# Revit family: Hager-VEGAD-Surface_mounted-IP30-Without_Cover-With_DIN-Hosted-FR-fr
name_source: partatom
category: Electrical Equipment
units: mm (PartAtom-declared; Revit-internal decimal feet)

## family parameters
Cut with Voids When Loaded = No
Host = Face
Maintain Annotation Orientation = Yes
Panel Configuration = Two Columns, Circuits Across
Part Type = Panelboard
Room Calculation Point = No
Round Connector Dimension = Use Diameter
Shared = No

## types (10) — shared parameters
BC_MODEL_ID = 1547015
BC_OBJECT_ID = 513439
BC_OBJECT_VERSION = #3
Code hager = ADD-EC000214_EU
EF000003 - mode de pose = saillie
EF000007 - couleur = blanc
EF000008 - largeur = 550 mm  [stored 1.80446 ft]
EF000024 - résistant aux UV = No
EF000049 - profondeur = 193 mm  [stored 0.633202 ft]
EF000116 - numéro RAL = 9010
EF000118 - avec cadre/support de montage = No
EF000218 - profondeur d'encastrement = 193 mm  [stored 0.633202 ft]
EF000846 - largeur d'encastrement = 550 mm  [stored 1.80446 ft]
EF001062 - finition CEM = No
EF001088 - possibilité de montage en saillie = Yes
EF001134 - rail DIN = Yes
EF002950 - largeur en nombre de modules = 24
EF005474 - indice de protection (IP) = IP30
EF006244 - couvercle/porte transparent(e) = No
EF006306 - avec serrure = No
EF009212 - finition du couvercle = avec échancrure
EF015776 - borne de mise à la terre = Yes
EF015777 - borne à conducteur neutre = No
EF015941 - porte pour transmission du signal = No
ETIM class code = EC000214
ETIM class name = Small distribution board
HG000001-nombre de colonnes = 1
HG000002-avec porte = No
HG000003-Gamme = VEGAD
HG000005-Epaisseur = 2 mm  [stored 0.00656168 ft]
HG000006-Encastré = No
HG000009-Porte à double battant = No
HG000010-Portes asymétriques = No
HG000011-Rangées du bas vides = No
HG000012-Angle de pivotement de la porte = 90.00°
HG000013-Porte à gauche = No
HG000014-Porte à droite = Yes
HG000015-Visibilité de l'emprise de la porte = Yes
HG000016-Visibilité de la porte 3D = Yes
HG000017-Distance entre pôles = 18 mm  [stored 0.0590551 ft]
HG000060-RAL-number = 9010
HG000099-ID modèle Onfly = 507532
HGEF0002950-largeur en nombre de modules = 24
Manufacturer = Hager
Name = VEGAD-Surface_mounted-IP30-Without_Cover-With_DIN-FR
Name BIM&CO = Electricity
Name hager = ADD_Enclosures_EC000214
Uniformat = Low Tension Service & Dist.
Uniformat code = D501001
zero-valued in all types: Default Elevation, EF001131 - profondeur intérieure, HG000007-Nombre de colonnes vides

## per-type parameters (varying)
| type | BC_VARIANT_ID | EF000040 - hauteur | EF000266 - nombre de rangées | EF000332 - hauteur d'encastrement | HG000004-Référence fabricant | HG000008-Nombre de rangées vides | HGEF000266-Nombre de rangées |
| VEGAD-Surface_mounted_W550_H450_D193_24_Modular_Spacing-FD22DN | 1173903 | 450 mm  [stored 1.47638 ft] | 2 | 450 mm  [stored 1.47638 ft] | FD22DN | 0 | 2 |
| VEGAD-Surface_mounted_W550_H600_D193_24_Modular_Spacing-FD32DN | 1173904 | 600 mm | 3 | 600 mm | FD32DN | 0 | 3 |
| VEGAD-Surface_mounted_W550_H750_D193_24_Modular_Spacing-FD42AN | 1173905 | 750 mm  [stored 2.46063 ft] | 4 | 750 mm  [stored 2.46063 ft] | FD42AN | 2 | 4 |
| VEGAD-Surface_mounted_W550_H750_D193_24_Modular_Spacing-FD42DN | 1173906 | 750 mm  [stored 2.46063 ft] | 4 | 750 mm  [stored 2.46063 ft] | FD42DN | 0 | 4 |
| VEGAD-Surface_mounted_W550_H900_D193_24_Modular_Spacing-FD52AN | 1173907 | 900 mm  [stored 2.95276 ft] | 5 | 900 mm  [stored 2.95276 ft] | FD52AN | 2 | 5 |
| VEGAD-Surface_mounted_W550_H900_D193_24_Modular_Spacing-FD52DN | 1173908 | 900 mm  [stored 2.95276 ft] | 5 | 900 mm  [stored 2.95276 ft] | FD52DN | 0 | 5 |
| VEGAD-Surface_mounted_W550_H1050_D193_24_Modular_Spacing-FD62AN | 1173909 | 1050 mm | 6 | 1050 mm | FD62AN | 2 | 6 |
| VEGAD-Surface_mounted_W550_H1050_D193_24_Modular_Spacing-FD62DN | 1173910 | 1050 mm | 6 | 1050 mm | FD62DN | 0 | 6 |
| VEGAD-Surface_mounted_W550_H1200_D193_24_Modular_Spacing-FD72AN | 1173911 | 1200 mm  [stored 3.93701 ft] | 7 | 1200 mm  [stored 3.93701 ft] | FD72AN | 2 | 7 |
| VEGAD-Surface_mounted_W550_H1200_D193_24_Modular_Spacing-FD72DN | 1173912 | 1200 mm  [stored 3.93701 ft] | 7 | 1200 mm  [stored 3.93701 ft] | FD72DN | 0 | 7 |

note: column(s) folded — value = type name in every type: Reference

note: [stored X ft] marks values corroborated as IEEE doubles in the binary element streams (Revit-internal decimal feet)

## geometry (parser evidence)
native form markers: Sweep x16
no freeform markers — native parametric forms only
